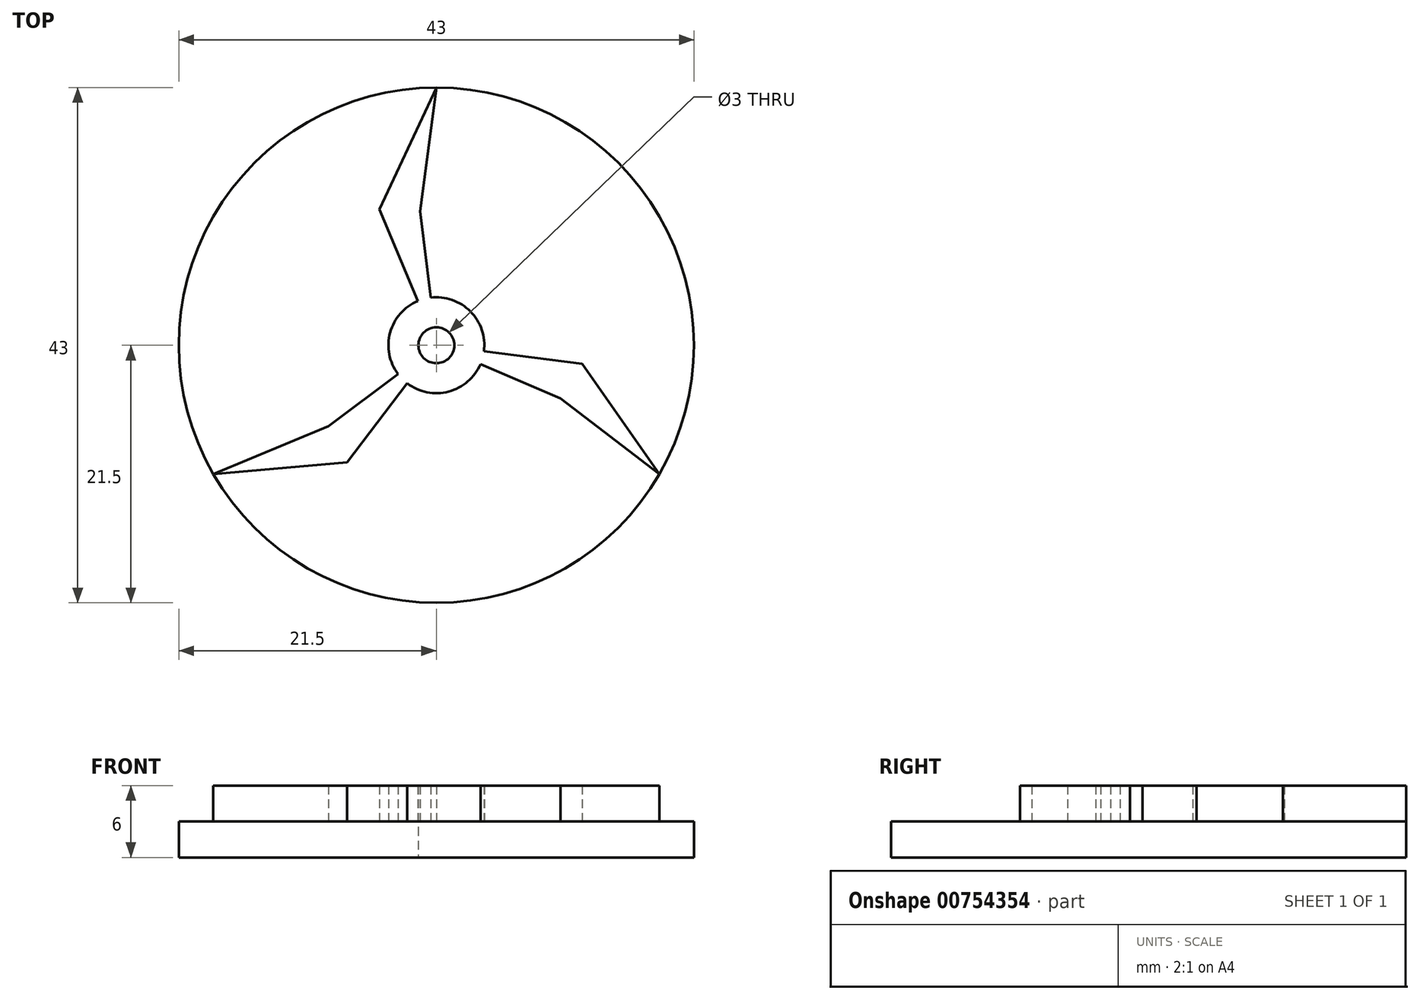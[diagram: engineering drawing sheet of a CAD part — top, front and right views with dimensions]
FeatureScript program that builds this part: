
annotation { "Feature Type Name" : "Feature", "Feature Type Description" : "" }
export const myFeature = defineFeature(function(context is Context, id is Id, definition is map)
    precondition{}
    {
        {
            var Q0;
            Q0=qCreatedBy(makeId("Top.planeOp"),FACE);
            var sketch = newSketch(context, id + "F0", { "sketchPlane" : qUnion([Q0])});
            skCircle(sketch, "E0", {"center": v(0, 0) * mm, "radius": 21.5 * mm});
            skSolve(sketch);
        }
        {
            var Q0;
            Q0 = qSketchRegion(id + "F0", true);
            extrude(context, id + "F1", {"entities" : qUnion([Q0]), "depth" : 3 * mm, "offsetDistance" : 25 * mm});
        }
        {
            var Q0;
            Q0=makeQuery(id+"F1.opExtrude","CAP_FACE",FACE,{"disambiguationData":[OSD([sQuery(id+"F0.wireOp",EDGE,"E0")])],"isStart":false});
            var sketch = newSketch(context, id + "F2", { "sketchPlane" : qUnion([Q0])});
            skLineSegment(sketch, "E1", {"start": v(0, 21.5) * mm, "end": v(-4.74, 11.32) * mm});
            skLineSegment(sketch, "E2", {"start": v(-4.74, 11.32) * mm, "end": v(-1.54, 3.7) * mm});
            skLineSegment(sketch, "E3", {"start": v(0, 21.5) * mm, "end": v(-1.35, 11.2) * mm});
            skLineSegment(sketch, "E4", {"start": v(-1.35, 11.2) * mm, "end": v(-0.48, 3.97) * mm});
            skLineSegment(sketch, "E5.1.0", {"start": v(-18.62, -10.75) * mm, "end": v(-9.02, -6.76) * mm});
            skLineSegment(sketch, "E5.1.1", {"start": v(-18.62, -10.75) * mm, "end": v(-7.44, -9.76) * mm});
            skLineSegment(sketch, "E5.1.2", {"start": v(-7.44, -9.76) * mm, "end": v(-2.42, -3.18) * mm});
            skLineSegment(sketch, "E5.1.3", {"start": v(-9.02, -6.76) * mm, "end": v(-3.2, -2.4) * mm});
            skLineSegment(sketch, "E5.2.0", {"start": v(18.62, -10.75) * mm, "end": v(10.37, -4.43) * mm});
            skLineSegment(sketch, "E5.2.1", {"start": v(18.62, -10.75) * mm, "end": v(12.18, -1.56) * mm});
            skLineSegment(sketch, "E5.2.2", {"start": v(12.18, -1.56) * mm, "end": v(3.97, -0.5) * mm});
            skLineSegment(sketch, "E5.2.3", {"start": v(10.37, -4.43) * mm, "end": v(3.68, -1.57) * mm});
            skPoint(sketch, "E5.center", {"position": v(0, 0) * mm});
            skArc(sketch, "E6", {"start": v(-1.54, 3.7) * mm, "mid": v(-3.86, 1.05) * mm, "end": v(-3.2, -2.4) * mm});
            skArc(sketch, "E7.trimOffspring", {"start": v(3.97, -0.5) * mm, "mid": v(2.84, 2.82) * mm, "end": v(-0.48, 3.97) * mm});
            skArc(sketch, "E8.trimOffspring", {"start": v(-2.42, -3.18) * mm, "mid": v(1.02, -3.87) * mm, "end": v(3.68, -1.57) * mm});
            skCircle(sketch, "E9", {"center": v(0, 0) * mm, "radius": 1 * mm});
            skSolve(sketch);
        }
        {
            var Q0;
            Q0 = qSketchRegion(id + "F2", true);
            extrude(context, id + "F3", {"entities" : qUnion([Q0]), "operationType" : NewBodyOperationType.ADD, "depth" : 3 * mm, "offsetDistance" : 25 * mm});
        }
        {
            var Q0;
            Q0=sQuery(id+"F0.wireOp",VERTEX,"E0.center");
            var Q1;
            Q1=makeQuery(id+"F1.opExtrude","SWEPT_BODY",BODY,{"disambiguationData":[OSD([sQuery(id+"F0.wireOp",EDGE,"E0")])]});
            hole(context, id + "F4", {"style" : HoleStyle.SIMPLE, "endStyle" : HoleEndStyle.THROUGH, "oppositeDirection" : true, "holeDiameter" : 3 * mm, "majorDiameter" : 5 * mm, "isTappedThrough" : true, "tappedDepth" : 12 * mm, "tapClearance" : 3, "locations" : qUnion([Q0]), "scope" : qUnion([Q1])});
        }
    });
